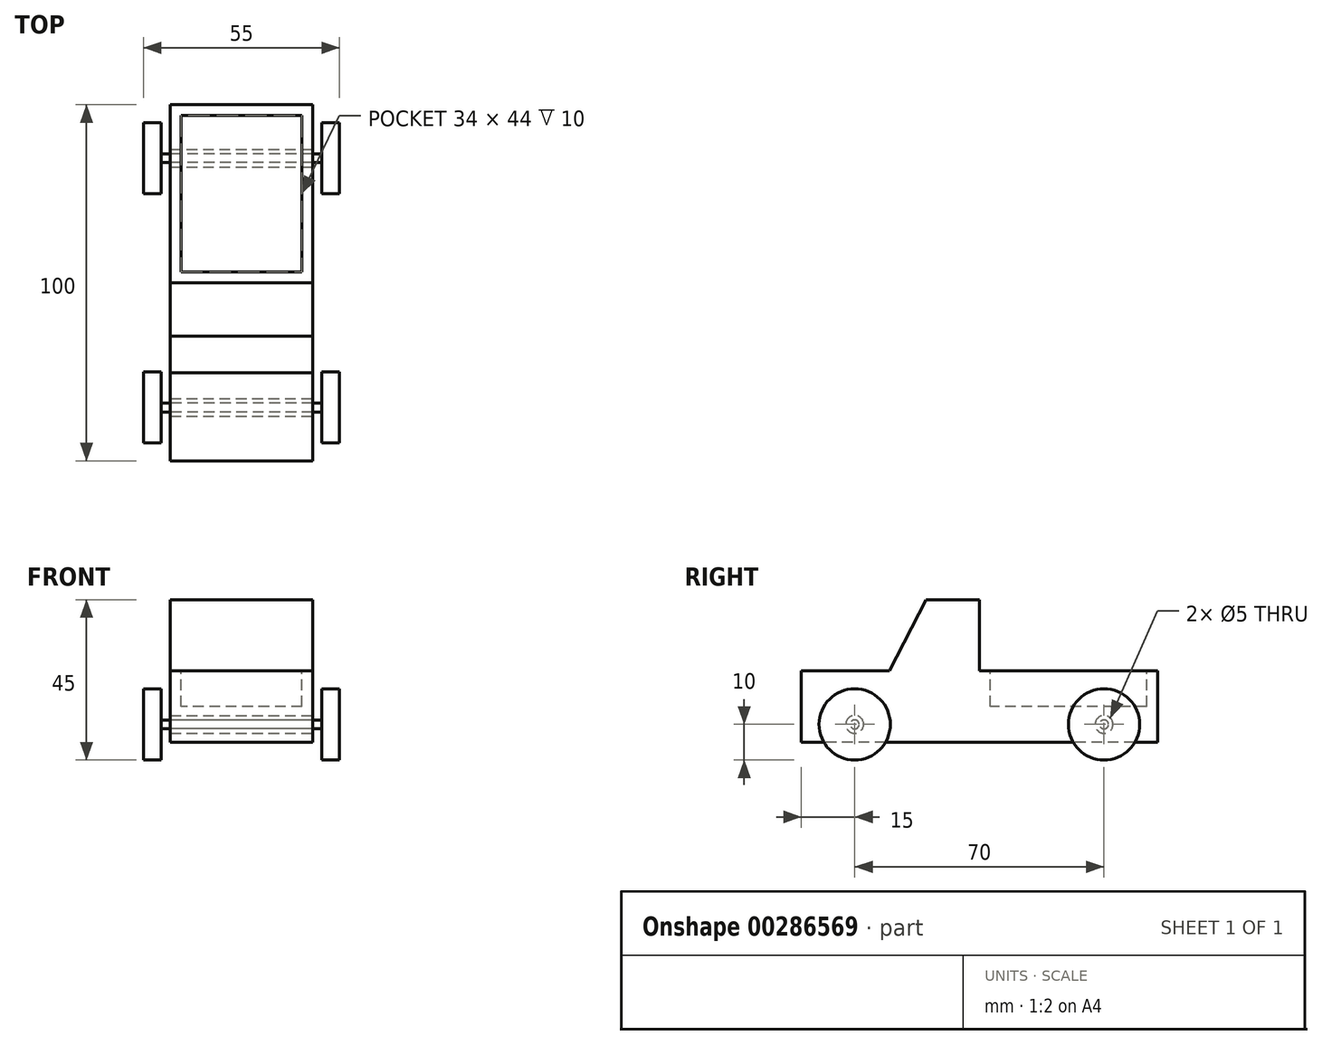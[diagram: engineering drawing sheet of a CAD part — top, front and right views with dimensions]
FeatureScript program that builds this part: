
annotation { "Feature Type Name" : "Feature", "Feature Type Description" : "" }
export const myFeature = defineFeature(function(context is Context, id is Id, definition is map)
    precondition{}
    {
        {
            var Q0;
            Q0=qCreatedBy(makeId("Right.planeOp"),FACE);
            var sketch = newSketch(context, id + "F0", { "sketchPlane" : qUnion([Q0])});
            skLineSegment(sketch, "E0.bottom", {"start": v(50, 10) * mm, "end": v(-50, 10) * mm});
            skLineSegment(sketch, "E0.top", {"start": v(50, -10) * mm, "end": v(-50, -10) * mm});
            skLineSegment(sketch, "E0.left", {"start": v(50, 10) * mm, "end": v(50, -10) * mm});
            skLineSegment(sketch, "E0.right", {"start": v(-50, 10) * mm, "end": v(-50, -10) * mm});
            skPoint(sketch, "E0.middle", {"position": v(0, 0) * mm});
            skSolve(sketch);
        }
        {
            var Q0;
            Q0 = qSketchRegion(id + "F0", true);
            extrude(context, id + "F1", {"entities" : qUnion([Q0]), "endBound" : BoundingType.SYMMETRIC, "depth" : 40 * mm});
        }
        {
            var Q0;
            Q0=makeQuery(id+"F1.opExtrude","CAP_FACE",FACE,{"disambiguationData":[OSD([sQuery(id+"F0.wireOp",EDGE,"E0.bottom"),sQuery(id+"F0.wireOp",EDGE,"E0.top"),sQuery(id+"F0.wireOp",EDGE,"E0.left"),sQuery(id+"F0.wireOp",EDGE,"E0.right")])],"isStart":false});
            var sketch = newSketch(context, id + "F2", { "sketchPlane" : qUnion([Q0])});
            skLineSegment(sketch, "E1", {"start": v(0, 10) * mm, "end": v(0, 30) * mm});
            skPoint(sketch, "E1.endSnap0", {"position": v(0, 10) * mm});
            skLineSegment(sketch, "E2", {"start": v(0, 30) * mm, "end": v(-15, 30) * mm});
            skLineSegment(sketch, "E3", {"start": v(-15, 30) * mm, "end": v(-25.3, 10) * mm});
            skLineSegment(sketch, "E4", {"start": v(-25.3, 10) * mm, "end": v(0, 10) * mm});
            skSolve(sketch);
        }
        {
            var Q0;
            Q0 = qSketchRegion(id + "F2", true);
            extrude(context, id + "F3", {"entities" : qUnion([Q0]), "operationType" : NewBodyOperationType.ADD, "oppositeDirection" : true, "depth" : 40 * mm});
        }
        {
            var Q0;
            Q0=makeQuery(id+"F3.boolean.opBoolean","MERGE",FACE,{"derivedFrom":[makeQuery(id+"F1.opExtrude","CAP_FACE",FACE,{"disambiguationData":[OSD([sQuery(id+"F0.wireOp",EDGE,"E0.bottom"),sQuery(id+"F0.wireOp",EDGE,"E0.top"),sQuery(id+"F0.wireOp",EDGE,"E0.left"),sQuery(id+"F0.wireOp",EDGE,"E0.right")])],"isStart":false}),makeQuery(id+"F3.opExtrude","CAP_FACE",FACE,{"disambiguationData":[OSD([sQuery(id+"F2.wireOp",EDGE,"E1"),sQuery(id+"F2.wireOp",EDGE,"E2"),sQuery(id+"F2.wireOp",EDGE,"E3"),sQuery(id+"F2.wireOp",EDGE,"E4")])],"isStart":true})]});
            var sketch = newSketch(context, id + "F4", { "sketchPlane" : qUnion([Q0])});
            skCircle(sketch, "E5", {"center": v(-35, -5) * mm, "radius": 2.5 * mm});
            skSolve(sketch);
        }
        {
            var Q0;
            Q0 = qSketchRegion(id + "F4", true);
            extrude(context, id + "F5", {"entities" : qUnion([Q0]), "operationType" : NewBodyOperationType.REMOVE, "endBound" : BoundingType.THROUGH_ALL, "oppositeDirection" : true, "depth" : 25 * mm});
        }
        {
            var Q0;
            Q0=makeQuery(id+"F3.boolean.opBoolean","MERGE",FACE,{"derivedFrom":[makeQuery(id+"F1.opExtrude","CAP_FACE",FACE,{"disambiguationData":[OSD([sQuery(id+"F0.wireOp",EDGE,"E0.bottom"),sQuery(id+"F0.wireOp",EDGE,"E0.top"),sQuery(id+"F0.wireOp",EDGE,"E0.left"),sQuery(id+"F0.wireOp",EDGE,"E0.right")])],"isStart":false}),makeQuery(id+"F3.opExtrude","CAP_FACE",FACE,{"disambiguationData":[OSD([sQuery(id+"F2.wireOp",EDGE,"E1"),sQuery(id+"F2.wireOp",EDGE,"E2"),sQuery(id+"F2.wireOp",EDGE,"E3"),sQuery(id+"F2.wireOp",EDGE,"E4")])],"isStart":true})]});
            var sketch = newSketch(context, id + "F6", { "sketchPlane" : qUnion([Q0])});
            skCircle(sketch, "E6", {"center": v(35, -5) * mm, "radius": 2.5 * mm});
            skSolve(sketch);
        }
        {
            var Q0;
            Q0 = qSketchRegion(id + "F6", true);
            extrude(context, id + "F7", {"entities" : qUnion([Q0]), "operationType" : NewBodyOperationType.REMOVE, "endBound" : BoundingType.THROUGH_ALL, "oppositeDirection" : true, "depth" : 25 * mm});
        }
        {
            var Q0;
            {var subQ2=sQuery(id+"F0.wireOp",EDGE,"E0.left");var subQ4=sQuery(id+"F0.wireOp",EDGE,"E0.bottom");Q0=makeQuery(id+"F3.boolean.opBoolean","SPLIT",FACE,{"disambiguationData":[TD([makeQuery(id+"F1.opExtrude","SWEPT_FACE",FACE,{"disambiguationData":[OSD([subQ2])]})])],"derivedFrom":makeQuery(id+"F1.opExtrude","SWEPT_FACE",FACE,{"disambiguationData":[OSD([subQ4])]})});}
            var sketch = newSketch(context, id + "F8", { "sketchPlane" : qUnion([Q0])});
            skLineSegment(sketch, "E7.0", {"start": v(-17, 47) * mm, "end": v(-17, 3) * mm});
            skLineSegment(sketch, "E7.1", {"start": v(17, 47) * mm, "end": v(-17, 47) * mm});
            skLineSegment(sketch, "E7.2", {"start": v(17, 47) * mm, "end": v(17, 3) * mm});
            skLineSegment(sketch, "E7.3", {"start": v(-17, 3) * mm, "end": v(17, 3) * mm});
            skSolve(sketch);
        }
        {
            var Q0;
            Q0 = qSketchRegion(id + "F8", true);
            extrude(context, id + "F9", {"entities" : qUnion([Q0]), "operationType" : NewBodyOperationType.REMOVE, "oppositeDirection" : true, "depth" : 10 * mm});
        }
        {
            var Q0;
            Q0=makeQuery(id+"F3.boolean.opBoolean","MERGE",FACE,{"derivedFrom":[makeQuery(id+"F1.opExtrude","CAP_FACE",FACE,{"disambiguationData":[OSD([sQuery(id+"F0.wireOp",EDGE,"E0.bottom"),sQuery(id+"F0.wireOp",EDGE,"E0.top"),sQuery(id+"F0.wireOp",EDGE,"E0.left"),sQuery(id+"F0.wireOp",EDGE,"E0.right")])],"isStart":false}),makeQuery(id+"F3.opExtrude","CAP_FACE",FACE,{"disambiguationData":[OSD([sQuery(id+"F2.wireOp",EDGE,"E1"),sQuery(id+"F2.wireOp",EDGE,"E2"),sQuery(id+"F2.wireOp",EDGE,"E3"),sQuery(id+"F2.wireOp",EDGE,"E4")])],"isStart":true})]});
            var sketch = newSketch(context, id + "F10", { "sketchPlane" : qUnion([Q0])});
            skCircle(sketch, "E8", {"center": v(-35, -5) * mm, "radius": 1.25 * mm});
            skSolve(sketch);
        }
        {
            var Q0;
            Q0 = qSketchRegion(id + "F10", true);
            extrude(context, id + "F11", {"entities" : qUnion([Q0]), "depth" : 2.5 * mm, "hasSecondDirection" : true, "secondDirectionOppositeDirection" : true, "secondDirectionDepth" : 42.5 * mm});
        }
        {
            var Q0;
            Q0=makeQuery(id+"F3.boolean.opBoolean","MERGE",FACE,{"derivedFrom":[makeQuery(id+"F1.opExtrude","CAP_FACE",FACE,{"disambiguationData":[OSD([sQuery(id+"F0.wireOp",EDGE,"E0.bottom"),sQuery(id+"F0.wireOp",EDGE,"E0.top"),sQuery(id+"F0.wireOp",EDGE,"E0.left"),sQuery(id+"F0.wireOp",EDGE,"E0.right")])],"isStart":false}),makeQuery(id+"F3.opExtrude","CAP_FACE",FACE,{"disambiguationData":[OSD([sQuery(id+"F2.wireOp",EDGE,"E1"),sQuery(id+"F2.wireOp",EDGE,"E2"),sQuery(id+"F2.wireOp",EDGE,"E3"),sQuery(id+"F2.wireOp",EDGE,"E4")])],"isStart":true})]});
            var sketch = newSketch(context, id + "F12", { "sketchPlane" : qUnion([Q0])});
            skCircle(sketch, "E9", {"center": v(35, -5) * mm, "radius": 1.25 * mm});
            skSolve(sketch);
        }
        {
            var Q0;
            Q0 = qSketchRegion(id + "F12", true);
            extrude(context, id + "F13", {"entities" : qUnion([Q0]), "depth" : 2.5 * mm, "hasSecondDirection" : true, "secondDirectionOppositeDirection" : true, "secondDirectionDepth" : 42.5 * mm});
        }
        {
            var Q0;
            Q0=makeQuery(id+"F11.opExtrude","CAP_FACE",FACE,{"disambiguationData":[OSD([sQuery(id+"F10.wireOp",EDGE,"E8")])],"isStart":false});
            var sketch = newSketch(context, id + "F14", { "sketchPlane" : qUnion([Q0])});
            skCircle(sketch, "E10", {"center": v(-35, -5) * mm, "radius": 10 * mm});
            skSolve(sketch);
        }
        {
            var Q0;
            Q0 = qSketchRegion(id + "F14", true);
            extrude(context, id + "F15", {"entities" : qUnion([Q0]), "operationType" : NewBodyOperationType.ADD, "depth" : 5 * mm});
        }
        {
            var Q0;
            Q0=makeQuery(id+"F11.opExtrude","CAP_FACE",FACE,{"disambiguationData":[OSD([sQuery(id+"F10.wireOp",EDGE,"E8")])],"isStart":true});
            var sketch = newSketch(context, id + "F16", { "sketchPlane" : qUnion([Q0])});
            skCircle(sketch, "E11", {"center": v(35, -5) * mm, "radius": 10 * mm});
            skSolve(sketch);
        }
        {
            var Q0;
            Q0 = qSketchRegion(id + "F16", true);
            extrude(context, id + "F17", {"entities" : qUnion([Q0]), "operationType" : NewBodyOperationType.ADD, "depth" : 5 * mm});
        }
        {
            var Q0;
            Q0=makeQuery(id+"F13.opExtrude","CAP_FACE",FACE,{"disambiguationData":[OSD([sQuery(id+"F12.wireOp",EDGE,"E9")])],"isStart":true});
            var sketch = newSketch(context, id + "F18", { "sketchPlane" : qUnion([Q0])});
            skCircle(sketch, "E12", {"center": v(-35, -5) * mm, "radius": 10 * mm});
            skSolve(sketch);
        }
        {
            var Q0;
            Q0 = qSketchRegion(id + "F18", true);
            extrude(context, id + "F19", {"entities" : qUnion([Q0]), "operationType" : NewBodyOperationType.ADD, "depth" : 5 * mm});
        }
        {
            var Q0;
            Q0=makeQuery(id+"F13.opExtrude","CAP_FACE",FACE,{"disambiguationData":[OSD([sQuery(id+"F12.wireOp",EDGE,"E9")])],"isStart":false});
            var sketch = newSketch(context, id + "F20", { "sketchPlane" : qUnion([Q0])});
            skCircle(sketch, "E13", {"center": v(35, -5) * mm, "radius": 10 * mm});
            skSolve(sketch);
        }
        {
            var Q0;
            Q0 = qSketchRegion(id + "F20", true);
            extrude(context, id + "F21", {"entities" : qUnion([Q0]), "operationType" : NewBodyOperationType.ADD, "depth" : 5 * mm});
        }
    });
